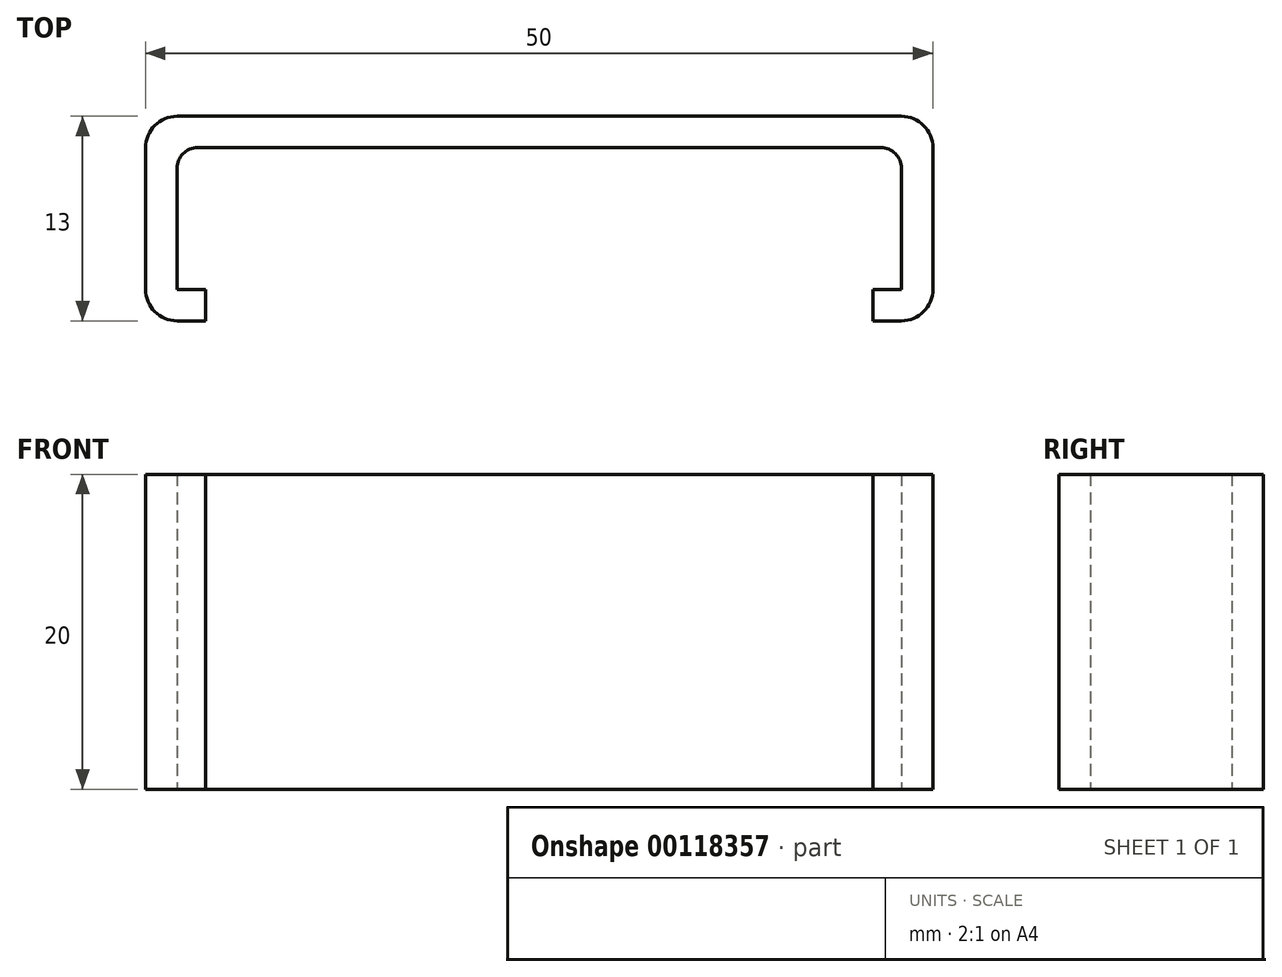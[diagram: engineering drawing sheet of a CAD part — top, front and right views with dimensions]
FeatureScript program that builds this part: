
annotation { "Feature Type Name" : "Feature", "Feature Type Description" : "" }
export const myFeature = defineFeature(function(context is Context, id is Id, definition is map)
    precondition{}
    {
        {
            var Q0;
            Q0=qCreatedBy(makeId("Top.planeOp"),FACE);
            var sketch = newSketch(context, id + "F0", { "sketchPlane" : qUnion([Q0])});
            skLineSegment(sketch, "E0.bottom", {"start": v(2, 0) * mm, "end": v(3.8, 0) * mm});
            skLineSegment(sketch, "E0.top", {"start": v(2, 13) * mm, "end": v(48, 13) * mm});
            skLineSegment(sketch, "E0.left", {"start": v(0, 2) * mm, "end": v(0, 11) * mm});
            skLineSegment(sketch, "E0.right", {"start": v(50, 2) * mm, "end": v(50, 11) * mm});
            skLineSegment(sketch, "E1.0", {"start": v(3.3, 11) * mm, "end": v(46.7, 11) * mm});
            skLineSegment(sketch, "E2.0", {"start": v(2, 2) * mm, "end": v(2, 9.7) * mm});
            skLineSegment(sketch, "E3.0", {"start": v(2, 2) * mm, "end": v(3.8, 2) * mm});
            skLineSegment(sketch, "E4.0", {"start": v(48, 2) * mm, "end": v(48, 9.7) * mm});
            skLineSegment(sketch, "E5.0", {"start": v(3.8, 0) * mm, "end": v(3.8, 2) * mm});
            skLineSegment(sketch, "E6.0", {"start": v(46.2, 0) * mm, "end": v(46.2, 2) * mm});
            skLineSegment(sketch, "E7.trimOffspring", {"start": v(46.2, 2) * mm, "end": v(48, 2) * mm});
            skLineSegment(sketch, "E8.trimOffspring", {"start": v(46.2, 0) * mm, "end": v(48, 0) * mm});
            skPoint(sketch, "E9.visualSharp", {"position": v(0, 13) * mm});
            skArc(sketch, "E9.filletArc", {"start": v(2, 13) * mm, "mid": v(0.59, 12.41) * mm, "end": v(0, 11) * mm});
            skPoint(sketch, "E10.visualSharp", {"position": v(50, 13) * mm});
            skArc(sketch, "E10.filletArc", {"start": v(50, 11) * mm, "mid": v(49.41, 12.41) * mm, "end": v(48, 13) * mm});
            skArc(sketch, "E11.filletArc", {"start": v(48, 9.7) * mm, "mid": v(47.62, 10.62) * mm, "end": v(46.7, 11) * mm});
            skArc(sketch, "E12.filletArc", {"start": v(3.3, 11) * mm, "mid": v(2.38, 10.62) * mm, "end": v(2, 9.7) * mm});
            skPoint(sketch, "E13.visualSharp", {"position": v(0, 0) * mm});
            skArc(sketch, "E13.filletArc", {"start": v(0, 2) * mm, "mid": v(0.59, 0.59) * mm, "end": v(2, 0) * mm});
            skPoint(sketch, "E14.visualSharp", {"position": v(50, 0) * mm});
            skArc(sketch, "E14.filletArc", {"start": v(48, 0) * mm, "mid": v(49.41, 0.59) * mm, "end": v(50, 2) * mm});
            skLineSegment(sketch, "E15.filletArc", {"start": v(48, 2) * mm, "end": v(48, 2) * mm});
            skSolve(sketch);
        }
        {
            var Q0;
            Q0 = qSketchRegion(id + "F0", true);
            extrude(context, id + "F1", {"entities" : qUnion([Q0]), "depth" : 20 * mm});
        }
    });
